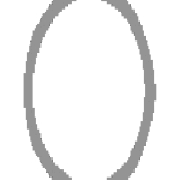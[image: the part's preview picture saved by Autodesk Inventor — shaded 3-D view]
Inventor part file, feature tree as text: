
AUTODESK INVENTOR PART (.ipt)
format: ipt  version: 2021 (Build 250183000, 183)  size: 112,128 bytes
history: native  units: in
note: dims shown in document units (in); Inventor stores cm internally (conversion verified against a paired STEP export)
features: other x4, sketch x3, plane x1
ambient origin geometry x8: Origin, YZ Plane, XZ Plane, XY Plane, X Axis, Y Axis, Z Axis, Center Point
bodies: Solid1 (feature_tree), Body (feature_tree)
feature tree (8):
  other  "Driven Length"
  other  "Frame Generator"
  other  "Start Plane"
  other  "End Plane"
  sketch  "Sketch"  dims[d2=6.7082in d4=-0.0in d5=6.7082in d6=0.12in d7=0.0in d8=90.0deg d9=6.7082in]
  sketch  "Sketch2"  dims[d0=1.0in]
  plane  "Work Plane3"
  sketch  "Sketch3"  dims[d1=0.065in]
